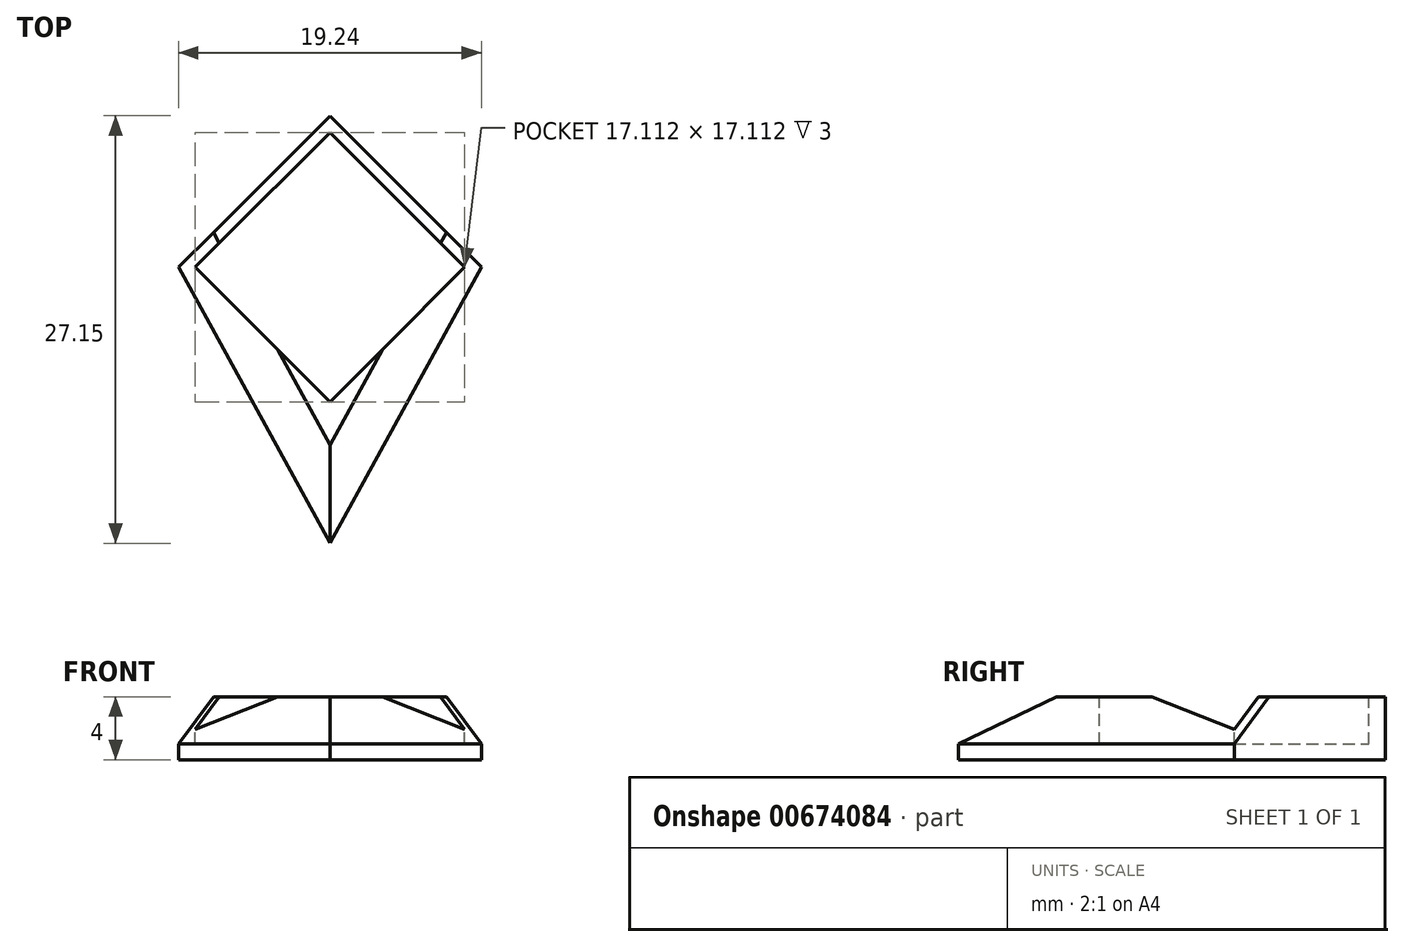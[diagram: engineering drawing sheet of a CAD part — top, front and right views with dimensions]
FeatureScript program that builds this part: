
annotation { "Feature Type Name" : "Feature", "Feature Type Description" : "" }
export const myFeature = defineFeature(function(context is Context, id is Id, definition is map)
    precondition{}
    {
        {
            var Q0;
            Q0=qCreatedBy(makeId("Top.planeOp"),FACE);
            var sketch = newSketch(context, id + "F0", { "sketchPlane" : qUnion([Q0])});
            skLineSegment(sketch, "E0.bottom", {"start": v(-6.8, -6.8) * mm, "end": v(6.8, -6.8) * mm});
            skLineSegment(sketch, "E0.top", {"start": v(-6.8, 6.8) * mm, "end": v(6.8, 6.8) * mm});
            skLineSegment(sketch, "E0.left", {"start": v(-6.8, -6.8) * mm, "end": v(-6.8, 6.8) * mm});
            skLineSegment(sketch, "E0.right", {"start": v(6.8, -6.8) * mm, "end": v(6.8, 6.8) * mm});
            skPoint(sketch, "E0.middle", {"position": v(0, 0) * mm});
            skSolve(sketch);
        }
        {
            var Q0;
            Q0=makeQuery(id+"F0.imprint","IMPRINT",FACE,{"disambiguationData":[TD([[makeQuery(id+"F0.imprint","IMPRINT",EDGE,{"derivedFrom":sQuery(id+"F0.wireOp",EDGE,"E0.bottom")}),1.0]])]});
            extrude(context, id + "F1", {"entities" : qUnion([Q0]), "depth" : 4 * mm, "offsetDistance" : 25 * mm});
        }
        {
            var Q0;
            Q0=makeQuery(id+"F1.opExtrude","CAP_FACE",FACE,{"disambiguationData":[OSD([sQuery(id+"F0.wireOp",EDGE,"E0.bottom"),sQuery(id+"F0.wireOp",EDGE,"E0.top"),sQuery(id+"F0.wireOp",EDGE,"E0.left"),sQuery(id+"F0.wireOp",EDGE,"E0.right")])],"isStart":false});
            var sketch = newSketch(context, id + "F2", { "sketchPlane" : qUnion([Q0])});
            skLineSegment(sketch, "E1.bottom", {"start": v(-6.05, -6.05) * mm, "end": v(6.05, -6.05) * mm});
            skLineSegment(sketch, "E1.top", {"start": v(-6.05, 6.05) * mm, "end": v(6.05, 6.05) * mm});
            skLineSegment(sketch, "E1.left", {"start": v(-6.05, -6.05) * mm, "end": v(-6.05, 6.05) * mm});
            skLineSegment(sketch, "E1.right", {"start": v(6.05, -6.05) * mm, "end": v(6.05, 6.05) * mm});
            skPoint(sketch, "E1.middle", {"position": v(0, 0) * mm});
            skSolve(sketch);
        }
        {
            var Q0;
            Q0=makeQuery(id+"F2.imprint","IMPRINT",FACE,{"disambiguationData":[TD([[makeQuery(id+"F2.imprint","IMPRINT",EDGE,{"derivedFrom":sQuery(id+"F2.wireOp",EDGE,"E1.bottom")}),1.0]])]});
            extrude(context, id + "F3", {"entities" : qUnion([Q0]), "operationType" : NewBodyOperationType.REMOVE, "oppositeDirection" : true, "depth" : 3 * mm, "offsetDistance" : 25 * mm});
        }
        {
            var Q0;
            Q0=qCreatedBy(makeId("Right.planeOp"),FACE);
            var sketch = newSketch(context, id + "F4", { "sketchPlane" : qUnion([Q0])});
            skLineSegment(sketch, "E2", {"start": v(0, 0) * mm, "end": v(0, 33.1) * mm});
            skSolve(sketch);
        }
        {
            var Q0;
            Q0=makeQuery(id+"F1.opExtrude","SWEPT_BODY",BODY,{"disambiguationData":[OSD([sQuery(id+"F0.wireOp",EDGE,"E0.bottom"),sQuery(id+"F0.wireOp",EDGE,"E0.top"),sQuery(id+"F0.wireOp",EDGE,"E0.left"),sQuery(id+"F0.wireOp",EDGE,"E0.right")])]});
            var Q1;
            Q1=sQuery(id+"F4.wireOp",EDGE,"E2");
            transform(context, id + "F5", {"entities" : qUnion([Q0]), "transformType" : TransformType.ROTATION, "transformAxis" : qUnion([Q1]), "angle" : 45 * degree, "makeCopy" : false});
        }
        {
            var Q0;
            Q0=makeQuery(id+"F1.opExtrude","CAP_FACE",FACE,{"disambiguationData":[OSD([sQuery(id+"F0.wireOp",EDGE,"E0.bottom"),sQuery(id+"F0.wireOp",EDGE,"E0.top"),sQuery(id+"F0.wireOp",EDGE,"E0.left"),sQuery(id+"F0.wireOp",EDGE,"E0.right")])],"isStart":true});
            var sketch = newSketch(context, id + "F6", { "sketchPlane" : qUnion([Q0])});
            skLineSegment(sketch, "E3", {"start": v(9.62, 0) * mm, "end": v(0, 17.53) * mm});
            skLineSegment(sketch, "E4", {"start": v(0, 17.53) * mm, "end": v(-9.62, 0) * mm});
            skSolve(sketch);
        }
        {
            var Q0;
            Q0=makeQuery(id+"F6.imprint","IMPRINT",FACE,{"disambiguationData":[TD([[makeQuery(id+"F6.imprint","IMPRINT",EDGE,{"derivedFrom":sQuery(id+"F6.wireOp",EDGE,"E3")}),1.0]])]});
            extrude(context, id + "F7", {"entities" : qUnion([Q0]), "operationType" : NewBodyOperationType.ADD, "oppositeDirection" : true, "depth" : 4 * mm, "offsetDistance" : 25 * mm});
        }
        {
            var Q0;
            Q0=makeQuery(id+"F7.opExtrude","CAP_EDGE",EDGE,{"disambiguationData":[OSD([sQuery(id+"F6.wireOp",EDGE,"E3")])],"isStart":false});
            var Q1;
            Q1=makeQuery(id+"F7.opExtrude","CAP_EDGE",EDGE,{"disambiguationData":[OSD([sQuery(id+"F6.wireOp",EDGE,"E4")])],"isStart":false});
            chamfer(context, id + "F8", {"entities" : qUnion([Q0, Q1]), "width" : 3 * mm, "tangentPropagation" : true});
        }
    });
